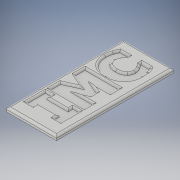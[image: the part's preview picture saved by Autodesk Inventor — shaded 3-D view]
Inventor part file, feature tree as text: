
AUTODESK INVENTOR PART (.ipt)
format: ipt  version: 2018 (Build 220112000, 112)  size: 370,688 bytes
history: native  units: in
note: dims shown in document units (in); Inventor stores cm internally (conversion verified against a paired STEP export)
features: fillet x5, sketch x3, extrude x2, emboss x1
ambient origin geometry x8: Origin, YZ Plane, XZ Plane, XY Plane, X Axis, Y Axis, Z Axis, Center Point
bodies: Solid1 (feature_tree)
feature tree (11):
  extrude  "Extrusion1"  Depth=7.0in
  emboss  "Emboss1"
  extrude  "Extrusion2"  Depth=0.1in TaperAngle=0.0deg
  fillet  "Fillet1"  Radius=0.125in
  fillet  "Fillet2"  Radius=0.125in
  fillet  "Fillet3"  Radius=0.125in
  fillet  "Fillet4"  Radius=0.125in
  fillet  "Fillet5"  Radius=0.125in
  sketch  "Sketch1"  dims[d0=3.0in d1=7.0in]
  sketch  "Sketch2"  dims[d2=0.125in d3=0.0in d4=0.1in d5=0.0in d6=0.125in d7=0.0in d8=0.125in d9=0.125in d10=0.125in d11=0.125in]
  sketch  "Sketch3"  dims[d12=0.1875in]
